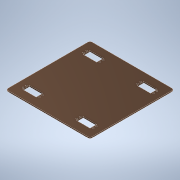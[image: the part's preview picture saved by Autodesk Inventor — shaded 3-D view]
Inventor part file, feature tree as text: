
AUTODESK INVENTOR PART (.ipt)
format: ipt  version: 2022.3 (Build 263350000, 350)  size: 208,384 bytes
history: native  units: in
note: dims shown in document units (in); Inventor stores cm internally (conversion verified against a paired STEP export)
features: extrude x2, sketch x2, fillet x1
ambient origin geometry x8: Origin, YZ Plane, XZ Plane, XY Plane, X Axis, Y Axis, Z Axis, Center Point
bodies: Solid1 (feature_tree)
feature tree (5):
  extrude  "Extrusion1"  Depth=10.0in
  fillet  "Fillet1"  Radius=0.125in
  extrude  "Extrusion2"  Depth=1.6in
  sketch  "Sketch1"  dims[d0=10.0in d1=10.0in d2=0.125in d3=0.0in]
  sketch  "Sketch2"  dims[d4=0.25in d5=1.6in d6=0.8in d8=1.0in d9=0.125in d10=0.0in d13=1.6in d14=0.8in d19=1.0in d20=1.0in d23=0.1719in d24=0.1719in d25=0.1719in d26=0.1719in d27=0.3878in d28=0.3878in d29=1.95in d30=1.95in d31=0.0in d32=0.0in d33=0.175in d34=0.2061in d35=1.6in d36=0.8in d37=0.1719in d38=0.1719in d39=0.1719in d40=0.1719in d41=0.3878in d42=0.3878in d43=1.95in d44=1.95in d45=0.0in d46=0.0in d47=0.175in d48=0.2061in d49=1.6in d50=0.8in d51=1.0in d52=1.0in d53=1.6in d54=0.8in d55=0.1719in d56=0.1719in d57=0.1719in d58=0.1719in d59=0.3878in d60=0.3878in d61=1.95in d62=1.95in d63=0.0in d64=0.0in d65=0.175in d66=0.2061in d67=1.6in d68=0.8in d69=1.6in d70=0.8in d71=0.1719in d72=0.1719in d73=0.1719in d74=0.1719in d75=0.3878in d76=0.3878in d77=1.95in d78=1.95in d79=0.0in d80=0.0in d81=0.175in d82=0.2061in d83=1.6in d84=0.8in d85=1.0in d86=1.0in d87=1.0in d88=1.0in d11=0.5in d12=0.0344in]
